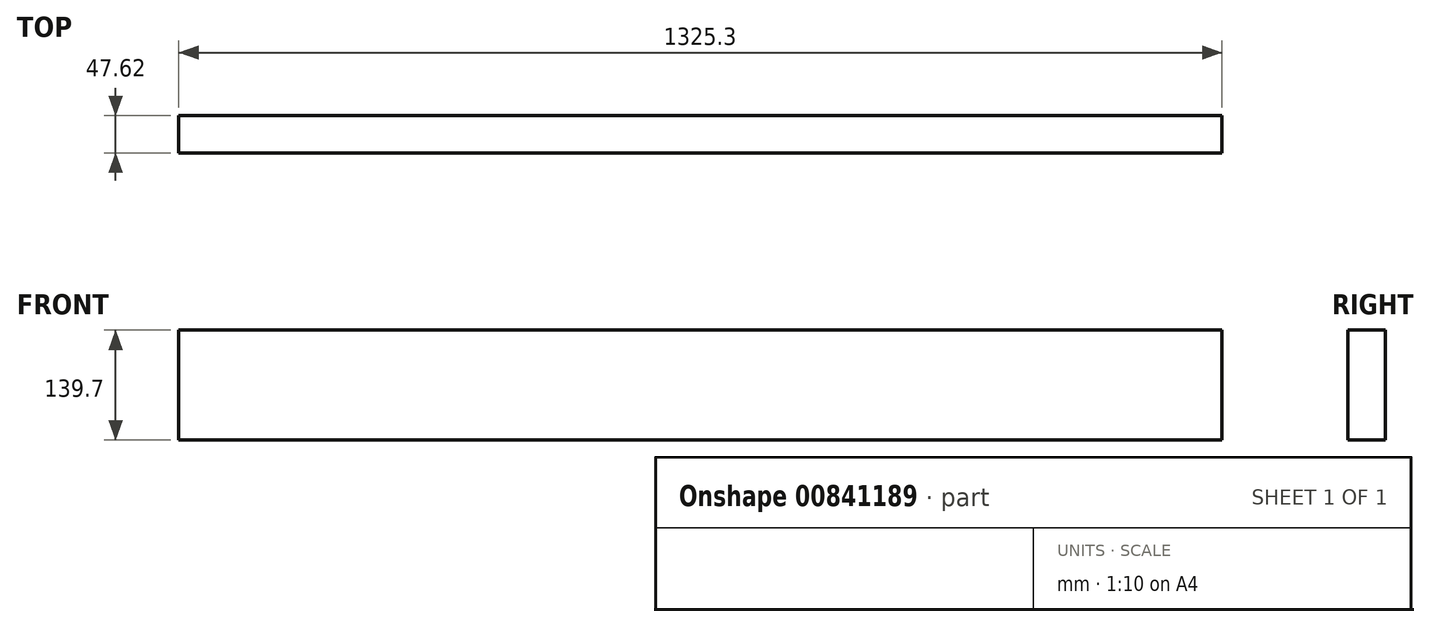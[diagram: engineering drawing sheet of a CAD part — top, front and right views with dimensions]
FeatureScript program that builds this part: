
annotation { "Feature Type Name" : "Feature", "Feature Type Description" : "" }
export const myFeature = defineFeature(function(context is Context, id is Id, definition is map)
    precondition{}
    {
        {
            var Q0;
            Q0=qCreatedBy(makeId("Right.planeOp"),FACE);
            var sketch = newSketch(context, id + "F0", { "sketchPlane" : qUnion([Q0])});
            skLineSegment(sketch, "E0.bottom", {"start": v(0, 0) * mm, "end": v(47.62, 0) * mm});
            skLineSegment(sketch, "E0.top", {"start": v(0, -139.7) * mm, "end": v(47.63, -139.7) * mm});
            skLineSegment(sketch, "E0.left", {"start": v(0, 0) * mm, "end": v(0, -139.7) * mm});
            skLineSegment(sketch, "E0.right", {"start": v(47.62, 0) * mm, "end": v(47.63, -139.7) * mm});
            skSolve(sketch);
        }
        {
            var Q0;
            Q0 = qSketchRegion(id + "F0", true);
            extrude(context, id + "F1", {"entities" : qUnion([Q0]), "depth" : 1325.3 * mm, "offsetDistance" : 25.4 * mm});
        }
    });
